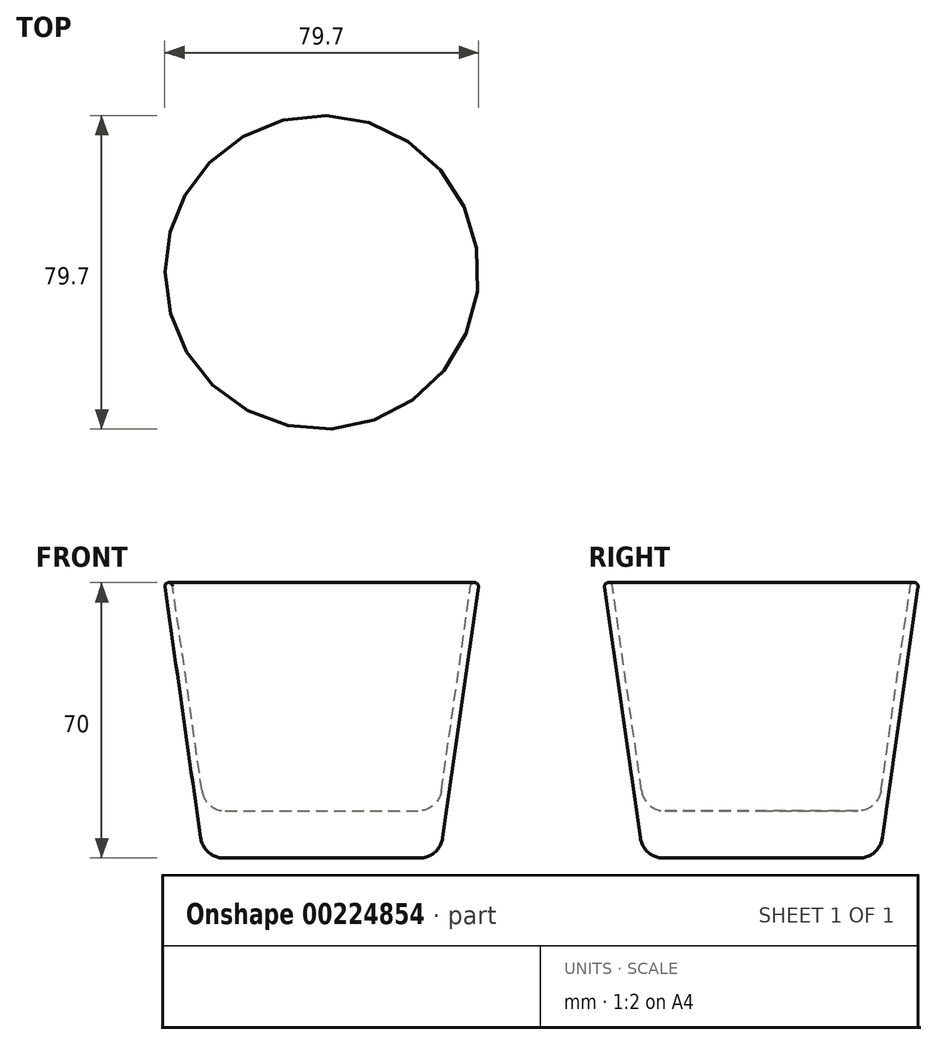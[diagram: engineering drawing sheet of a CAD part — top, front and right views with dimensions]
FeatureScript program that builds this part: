
annotation { "Feature Type Name" : "Feature", "Feature Type Description" : "" }
export const myFeature = defineFeature(function(context is Context, id is Id, definition is map)
    precondition{}
    {
        {
            var Q0;
            Q0=qCreatedBy(makeId("Front.planeOp"),FACE);
            var sketch = newSketch(context, id + "F0", { "sketchPlane" : qUnion([Q0])});
            skLineSegment(sketch, "E0", {"start": v(0, 0) * mm, "end": v(0, 83.51) * mm, "construction": true});
            skLineSegment(sketch, "E1", {"start": v(0, 0) * mm, "end": v(24.8, 0) * mm});
            skLineSegment(sketch, "E2", {"start": v(30.74, 5.15) * mm, "end": v(39.84, 68.86) * mm});
            skPoint(sketch, "E3.visualSharp", {"position": v(30, 0) * mm});
            skArc(sketch, "E3.filletArc", {"start": v(24.8, 0) * mm, "mid": v(28.73, 1.47) * mm, "end": v(30.74, 5.15) * mm});
            skLineSegment(sketch, "E4.0", {"start": v(30.43, 17.15) * mm, "end": v(37.86, 69.14) * mm});
            skLineSegment(sketch, "E5.0", {"start": v(0, 12) * mm, "end": v(24.5, 12) * mm});
            skArc(sketch, "E6.filletArc", {"start": v(24.5, 12) * mm, "mid": v(28.42, 13.47) * mm, "end": v(30.43, 17.15) * mm});
            skArc(sketch, "E7", {"start": v(39.84, 68.86) * mm, "mid": v(38.99, 69.99) * mm, "end": v(37.86, 69.14) * mm});
            skPoint(sketch, "E8.orphan", {"position": v(40, 70) * mm});
            skLineSegment(sketch, "E9", {"start": v(0, 12) * mm, "end": v(0, 0) * mm});
            skSolve(sketch);
        }
        {
            var Q0;
            Q0 = qSketchRegion(id + "F0", true);
            var Q1;
            Q1=sQuery(id+"F0.wireOp",EDGE,"E0");
            revolve(context, id + "F1", {"entities" : qUnion([Q0]), "axis" : qUnion([Q1]), "revolveType" : RevolveType.FULL});
        }
    });
